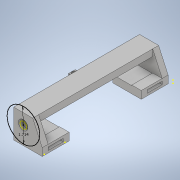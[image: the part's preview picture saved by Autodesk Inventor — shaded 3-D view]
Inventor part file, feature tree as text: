
AUTODESK INVENTOR PART (.ipt)
format: ipt  version: 2020 (Build 240168000, 168)  size: 588,288 bytes
history: native  units: in
note: dims shown in document units (in); Inventor stores cm internally (conversion verified against a paired STEP export)
features: sketch x30, extrude x19, fillet x5, hole x4
ambient origin geometry x8: Origin, YZ Plane, XZ Plane, XY Plane, X Axis, Y Axis, Z Axis, Center Point
bodies: Solid1 (feature_tree)
feature tree (58):
  sketch  "Sketch1"  dims[d6=0.3in d7=0.0in d10=1.5in d11=0.0in]
  sketch  "Sketch2"  dims[d19=0.125in d20=0.1575in d21=0.7874in]
  extrude  "Extrusion1"  Depth=1.5in TaperAngle=0.0deg
  sketch  "Sketch3"  dims[d22=0.0in d23=0.1215in]
  extrude  "Extrusion2"  Depth=0.7874in
  fillet  "Fillet1"  Radius=0.7874in
  extrude  "Extrusion3"  Depth=0.1215in
  extrude  "Extrusion4"  Depth=1.25in TaperAngle=0.0deg
  extrude  "Extrusion5"  Depth=1.25in TaperAngle=0.0deg
  hole  "Hole3"  [1 undecoded]
  hole  "Hole4"  [1 undecoded]
  hole  "Hole5"  [1 undecoded]
  extrude  "Extrusion6"  Depth=0.25in
  fillet  "Fillet2"  Radius=0.25in
  fillet  "Fillet3"  Radius=6.0in
  hole  "Hole6"  [1 undecoded]
  extrude  "Extrusion7"  Depth=0.5in TaperAngle=0.0deg
  extrude  "Extrusion8"  Depth=0.05in
  fillet  "Fillet4"  Radius=0.85in
  extrude  "Extrusion9"  Depth=0.05in
  sketch  "Sketch18"  dims[d87=0.85in d88=0.0in d89=0.05in]
  sketch  "Sketch19"  dims[d90=1.0in d91=6.6875in d92=0.0in]
  extrude  "Extrusion10"  Depth=1.0in TaperAngle=0.0deg
  extrude  "Extrusion11"  Depth=0.1181in TaperAngle=0.0deg
  sketch  "Sketch22"  dims[d98=0.325in d99=0.0in d100=1.413in]
  extrude  "Extrusion12"  Depth=0.25in
  extrude  "Extrusion13"  Depth=1.413in
  extrude  "Extrusion14"  Depth=1.413in
  extrude  "Extrusion15"  Depth=0.5in TaperAngle=0.0deg
  sketch  "Sketch27"  dims[d111=0.15in d112=0.35in d113=6.0in d114=0.0in]
  extrude  "Extrusion16"  Depth=0.125in
  extrude  "Extrusion17"  Depth=0.35in
  extrude  "Extrusion18"  Depth=0.35in
  fillet  "Fillet5"  Radius=6.0in
  extrude  "Extrusion19"  Depth=3.799in TaperAngle=0.0deg
  sketch  "Sketch32"  dims[d123=0.1in d124=0.3125in d125=0.0in d126=0.1in d127=0.23in d128=0.35in d129=0.1875in d130=0.0in d12=1.0in d13=1.0in d14=1.0in d15=0.15in d16=0.25in d17=0.375in d18=0.5635in d131=0.5in d132=0.0344in]
  sketch  "Sketch4"  dims[d24=0.1215in d25=1.25in d26=0.0in]
  sketch  "Sketch6"  dims[d28=0.0in d29=1.25in d30=0.0in]
  sketch  "Sketch7"  dims[d31=0.1215in d32=0.1215in]
  sketch  "Sketch8"  dims[d33=2.919in d35=1.25in d36=0.0in]
  sketch  "Sketch10"  dims[d37=1.25in d38=0.3125in]
  sketch  "Sketch11"  dims[d40=0.3125in d41=0.25in d42=0.25in d50=6.0in]
  sketch  "Sketch12"  dims[d51=0.35in d52=0.75in d53=0.375in d54=0.25in d55=0.5635in d56=1.0in d57=0.8108in]
  sketch  "Sketch13"  dims[d58=0.5in d59=0.75in d60=0.375in d61=0.25in d62=0.5635in d63=0.1875in d64=0.8108in]
  sketch  "Sketch14"  dims[d65=0.5in d66=0.75in d67=0.375in d68=0.25in d69=0.5635in d70=0.1875in d71=0.8108in d72=2.95in]
  sketch  "Sketch15"  dims[d73=2.95in d74=0.5in d75=0.0in]
  sketch  "Sketch16"  dims[d76=0.05in d77=0.05in]
  sketch  "Sketch17"  dims[d78=0.25in d79=0.75in d80=0.375in d81=0.25in d82=0.5635in d83=0.1875in d84=0.8108in d85=0.85in d86=0.0in]
  sketch  "Sketch20"  dims[d93=1.7143in d94=0.1181in d95=0.0in]
  sketch  "Sketch21"  dims[d96=0.25in d97=0.25in]
  sketch  "Sketch23"  dims[d101=0.401in d102=1.413in]
  sketch  "Sketch24"  dims[d103=0.401in d104=0.5in d105=0.0in]
  sketch  "Sketch25"  dims[d106=1.125in d107=0.0in d108=0.125in]
  sketch  "Sketch26"  dims[d109=0.15in d110=0.35in]
  sketch  "Sketch28"  dims[d115=3.799in d116=0.4375in d117=0.0in]
  sketch  "Sketch29"  dims[d118=0.3125in d119=0.0in]
  sketch  "Sketch30"  dims[d120=0.3125in d121=0.0in]
  sketch  "Sketch31"  dims[d122=0.1in]
note: 4 required parameter values undecoded (feature->parameter linkage not recoverable at this tier; creation-order binding heuristic only, values carry confidence <= 0.55)
